# Revit family: QF_HOSHIZAKI_HNC-210BE-R-BLH
name_source: partatom
category: Specialty Equipment
revit_build: Autodesk Revit 2016 (Build: 20150220_1215(x64)
units: mm (PartAtom-declared; Revit-internal decimal feet)

## family parameters
Always vertical = Yes
Cut with Voids When Loaded = No
OmniClass Number = 23.40.40.14
OmniClass Title = Food Service Equipment
Part Type = Normal
Room Calculation Point = No
Round Connector Dimension = Use Diameter
Shared = No
Work Plane-Based = No

## types (1)
- HNC-210BE-R-BLH_230V/1Ph/50Hz
    Accessory = No
    Apparent Power = 140 VA
    Assembly Code = E1090320
    Conn Conduit = No
    Cost = 0 $
    Cycle = 50 Hz
    Depth Actual = 345 mm
    Description = SUSHI CASE WITH LED LIGHTING, RIGHT SIDED - BLACK
    Electric power = 140 W
    FL Amps = 1 A
    Height Actual = 270 mm
    Indirect Waste Size = 51 mm
    Length Actual = 2100 mm
    Manufacturer = HOSHIZAKI
    Max Overcurrent Protection = 0 A
    Min Ckt Ampacity = 0 A
    Model = HNC-210BE-R-BLH
    Number of Poles = 2
    Phase = 1
    URL = www.hoshizaki-europe.com
    Volts = 230 V
    Weight = 47.00 kg

## geometry (parser evidence)
native form markers: Blend x14, Sweep x3
no freeform markers — native parametric forms only
